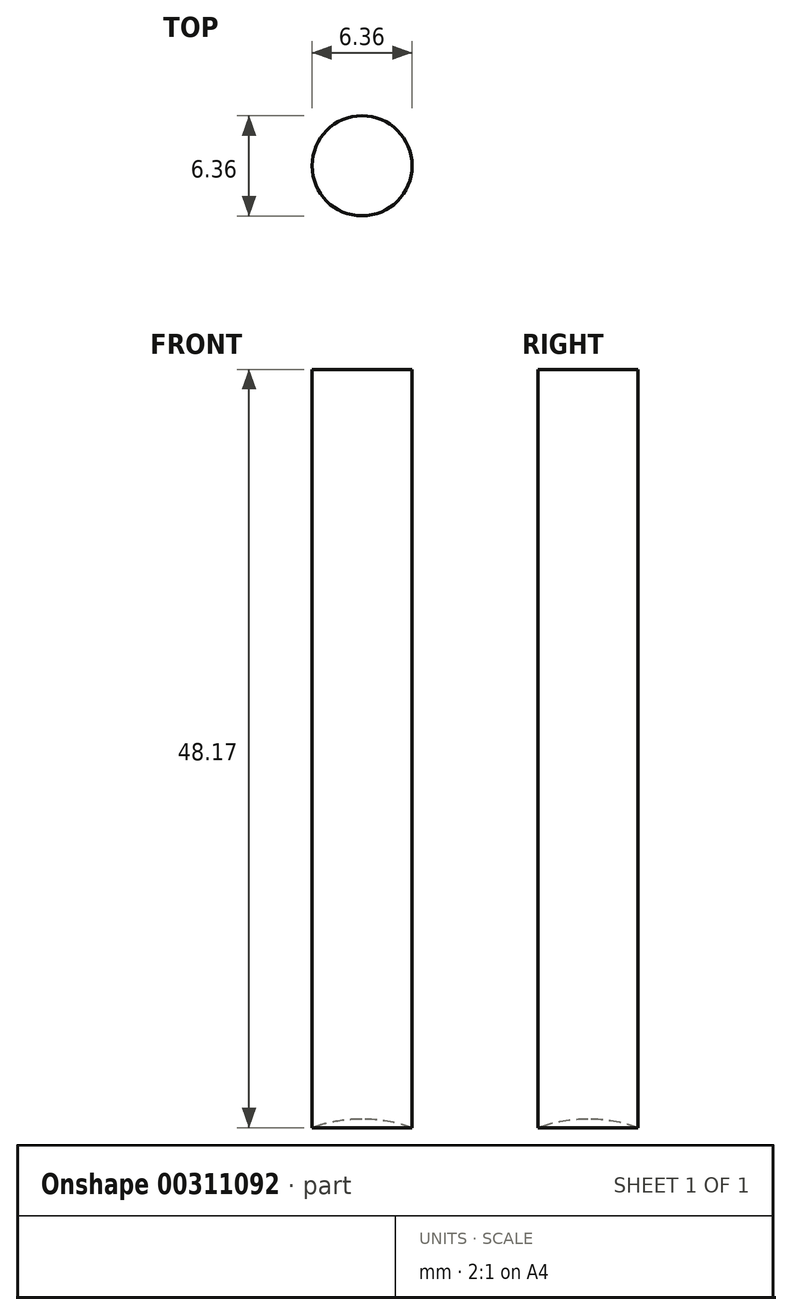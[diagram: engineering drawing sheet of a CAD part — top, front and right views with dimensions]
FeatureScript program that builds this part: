
annotation { "Feature Type Name" : "Feature", "Feature Type Description" : "" }
export const myFeature = defineFeature(function(context is Context, id is Id, definition is map)
    precondition{}
    {
        {
            var Q0;
            Q0=qCreatedBy(makeId("Front.planeOp"),FACE);
            var sketch = newSketch(context, id + "F0", { "sketchPlane" : qUnion([Q0])});
            skArc(sketch, "E0", {"start": v(0, 9.53) * mm, "mid": v(-9.53, 0) * mm, "end": v(0, -9.53) * mm});
            skLineSegment(sketch, "E1", {"start": v(0, -9.53) * mm, "end": v(0, 9.53) * mm});
            skSolve(sketch);
        }
        {
            var Q0;
            Q0=qCreatedBy(makeId("Top.planeOp"),FACE);
            var sketch = newSketch(context, id + "F1", { "sketchPlane" : qUnion([Q0])});
            skCircle(sketch, "E2", {"center": v(0, 0) * mm, "radius": 9.53 * mm});
            skSolve(sketch);
        }
        {
            var Q0;
            Q0=makeQuery(id+"F0.imprint","IMPRINT",FACE,{"disambiguationData":[TD([[makeQuery(id+"F0.imprint","IMPRINT",EDGE,{"derivedFrom":sQuery(id+"F0.wireOp",EDGE,"E0")}),1.0]])]});
            var Q1;
            Q1=sQuery(id+"F1.wireOp",EDGE,"E2");
            revolve(context, id + "F2", {"entities" : qUnion([Q0]), "axis" : qUnion([Q1]), "revolveType" : RevolveType.FULL});
        }
        {
            var Q0;
            Q0=qCreatedBy(makeId("Top.planeOp"),FACE);
            cPlane(context, id + "F3", {"entities" : qUnion([Q0]), "cplaneType" : CPlaneType.OFFSET, "offset" : 6.35 * mm, "width" : 152.4 * mm, "height" : 152.4 * mm});
        }
        {
            var Q0;
            Q0=qCreatedBy(id+"F3.planeOp",FACE);
            var sketch = newSketch(context, id + "F4", { "sketchPlane" : qUnion([Q0])});
            skCircle(sketch, "E3", {"center": v(0, 0) * mm, "radius": 3.18 * mm});
            skSolve(sketch);
        }
        {
            var Q0;
            Q0=qSketchRegion(id+"F4",true);
            extrude(context, id + "F5", {"entities" : qUnion([Q0]), "depth" : 50.8 * mm});
        }
        {
            var Q0;
            Q0=makeQuery(id+"F2.opRevolve","SWEPT_BODY",BODY,{"disambiguationData":[OSD([sQuery(id+"F0.wireOp",EDGE,"E0"),sQuery(id+"F0.wireOp",EDGE,"E1")])]});
            var Q1;
            Q1=makeQuery(id+"F5.opExtrude","SWEPT_BODY",BODY,{"disambiguationData":[OSD([sQuery(id+"F4.wireOp",EDGE,"E3")])]});
            booleanBodies(context, id + "F6", {"operationType" : BooleanOperationType.SUBTRACTION, "tools" : qUnion([Q0]), "targets" : qUnion([Q1])});
        }
    });
